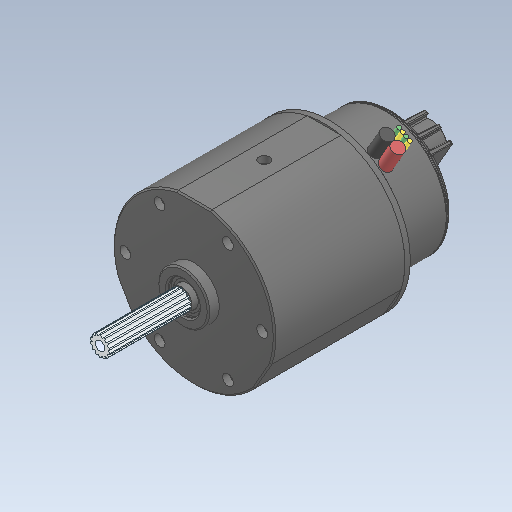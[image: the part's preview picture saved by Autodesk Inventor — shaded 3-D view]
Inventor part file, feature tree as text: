
AUTODESK INVENTOR PART (.ipt)
format: ipt  version: 2020 (Build 240168000, 168)  size: 1,227,776 bytes
history: native  units: in
note: dims shown in document units (in); Inventor stores cm internally (conversion verified against a paired STEP export)
features: fillet x4, other x2, chamfer x1
ambient origin geometry x8: Origin, YZ Plane, XZ Plane, XY Plane, X Axis, Y Axis, Z Axis, Center Point
bodies: Solid1 (feature_tree), Solid2 (feature_tree), Solid3 (feature_tree), Solid4 (feature_tree), Solid5 (feature_tree), Solid6 (feature_tree), Solid7 (feature_tree)
feature tree (7):
  chamfer  "Chamfer3"  [1 undecoded]
  other  "Boss-Extrude10"
  fillet  "Fillet4"  [1 undecoded]
  fillet  "Fillet3"  [1 undecoded]
  fillet  "Fillet5"  [1 undecoded]
  fillet  "Fillet6"  [1 undecoded]
  other  "#8-32 Tapped Hole1"
note: 5 required parameter values undecoded (feature->parameter linkage not recoverable at this tier; creation-order binding heuristic only, values carry confidence <= 0.55)
